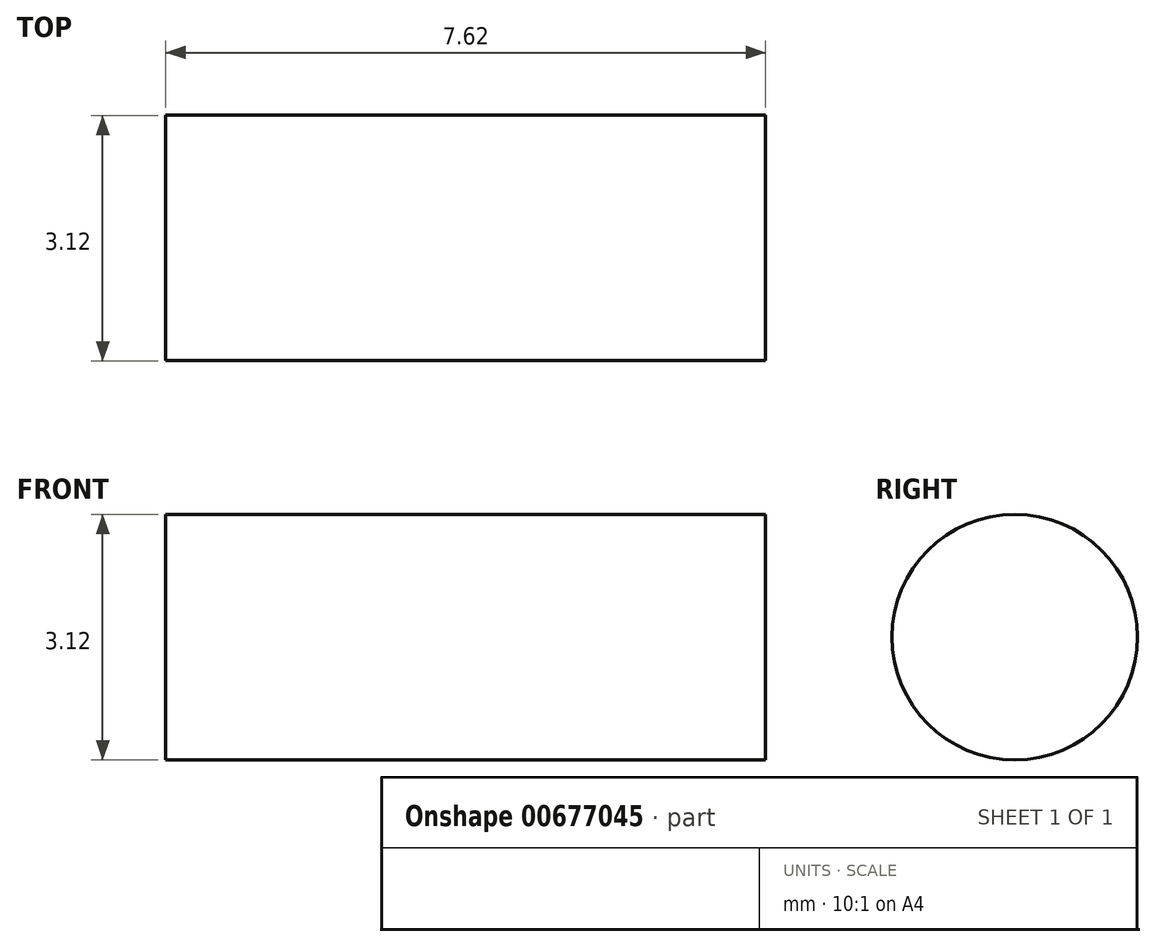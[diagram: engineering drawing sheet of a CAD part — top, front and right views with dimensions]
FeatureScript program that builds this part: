
annotation { "Feature Type Name" : "Feature", "Feature Type Description" : "" }
export const myFeature = defineFeature(function(context is Context, id is Id, definition is map)
    precondition{}
    {
        {
            var Q0;
            Q0=qCreatedBy(makeId("Right.planeOp"),FACE);
            var sketch = newSketch(context, id + "F0", { "sketchPlane" : qUnion([Q0])});
            skCircle(sketch, "E0", {"center": v(-2.39, 10.16) * mm, "radius": 1.56 * mm});
            skSolve(sketch);
        }
        {
            var Q0;
            Q0=makeQuery(id+"F0.imprint","IMPRINT",FACE,{"disambiguationData":[TD([[makeQuery(id+"F0.imprint","IMPRINT",EDGE,{"derivedFrom":sQuery(id+"F0.wireOp",EDGE,"E0")}),1.0]])]});
            extrude(context, id + "F1", {"entities" : qUnion([Q0]), "depth" : 7.62 * mm, "offsetDistance" : 25.4 * mm});
        }
    });
